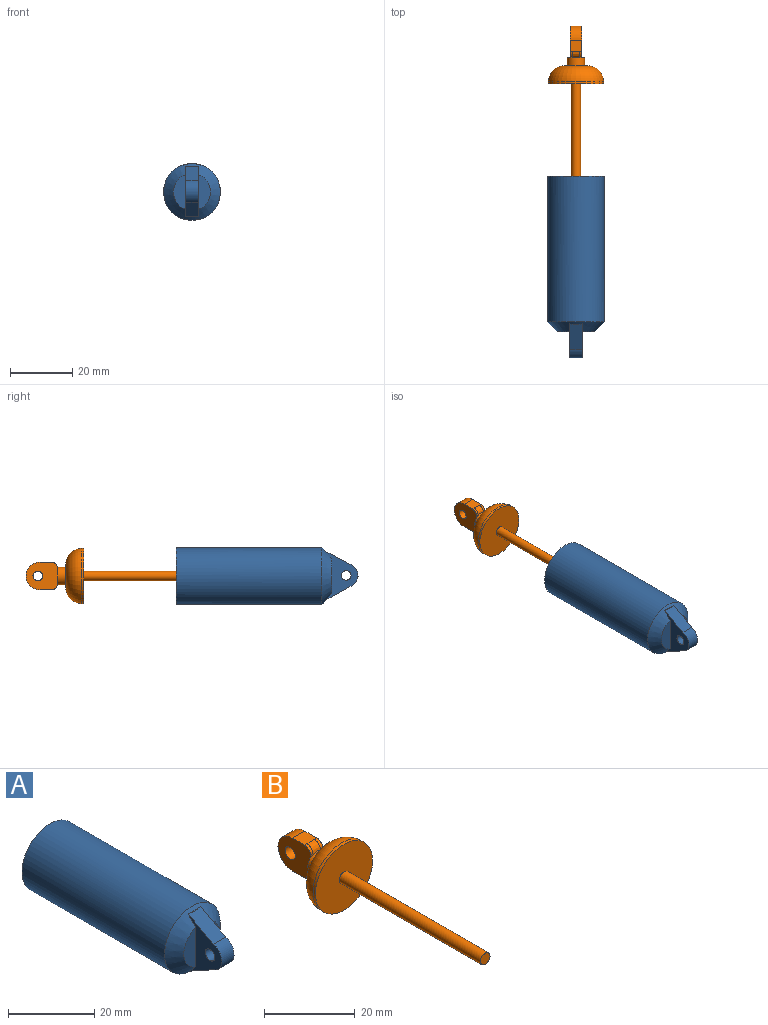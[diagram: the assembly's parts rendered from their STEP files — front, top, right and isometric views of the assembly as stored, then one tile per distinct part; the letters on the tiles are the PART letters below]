
ASSEMBLY  parts=2 mates=1
PART A: 15 faces, bbox 18.4x58.7x18.4 mm
  f0: plane 16.27x11.16mm, normal (1,0,0), area 70.3mm2, adj f1,f3,f7,f8,f9,f10
  f1: plane 11.23x3.94mm, normal (0,-1,0), area 32.2mm2, adj f0,f3
  f2: plane 11.23x3.94mm, normal (0,-1,0), area 32.2mm2, adj f3,f6
  f3: cone r=5.97mm half-angle=45deg, axis (0,1,0), area 187.2mm2, adj f0,f1,f2,f4,f6,f11,f12
  f4: cylinder r=9.14mm len=46.86mm, axis (0,1,0), area 2692.4mm2, adj f3,f5
  f5: plane 18.29x18.29mm, normal (0,1,0), area 255.4mm2, adj f4,f13
  f6: plane 16.27x11.16mm, normal (-1,0,0), area 70.3mm2, adj f2,f3,f7,f8,f9,f10
  f7: cylinder r=1.56mm len=4.06mm, axis (1,0,0), area 39.9mm2, adj f0,f6
  f8: cylinder r=3.81mm len=7.26mm, axis (1,0,0), area 39.1mm2, adj f0,f6,f9,f10
  f9: plane 8.37x4.44mm, normal (0,-0.47,0.88), area 38.5mm2, adj f0,f6,f8,f11
  f10: plane 8.04x4.44mm, normal (0,-0.48,-0.88), area 37.3mm2, adj f0,f6,f8,f12
  f11: plane 4.08x0.26mm, normal (0,0,-1), area 0.7mm2, adj f3,f9
  f12: plane 4.08x0.27mm, normal (0,0,1), area 0.7mm2, adj f3,f10
  f13: cylinder r=1.52mm len=34.54mm, axis (0,1,0), area 330.8mm2, adj f5,f14
  f14: plane 3.05x3.05mm, normal (0,1,0), area 7.3mm2, adj f13
PART B: 29 faces, bbox 17.8x62.6x17.8 mm
  f0: plane 0.74x0.5mm, normal (0,-1,0), area 0.2mm2, adj f10,f15,f25
  f1: plane 0.74x0.5mm, normal (0,-1,0), area 0.2mm2, adj f10,f13,f22
  f2: plane 4.09x0.89mm, normal (0,1,0), area 2.5mm2, adj f10,f13
  f3: plane 4.09x0.89mm, normal (0,1,0), area 2.5mm2, adj f10,f15
  f4: cylinder r=1.5mm len=43.94mm, axis (0,-1,0), area 413.8mm2, adj f5,f8
  f5: plane 3x3mm, normal (0,-1,0), area 7.1mm2, adj f4
  f6: cylinder r=8.89mm len=17.78mm, axis (0,-1,0), area 41.1mm2, adj f8,f9
  f7: plane 7.62x7.62mm, normal (0,1,0), area 21.1mm2, adj f9,f10
  f8: plane 17.78x17.78mm, normal (0,-1,0), area 241.2mm2, adj f4,f6
  f9: torus R=3.81mm, axis (0,1,0), area 353.2mm2, adj f6,f7
  f10: cylinder r=2.79mm len=5.59mm, axis (0,-1,0), area 46.8mm2, adj f0,f1,f2,f3,f7,f11,f12,f21
  f11: plane 0.74x0.5mm, normal (0,-1,0), area 0.2mm2, adj f10,f13,f23
  f12: plane 0.74x0.5mm, normal (0,-1,0), area 0.2mm2, adj f10,f15,f20
  f13: plane 10.16x8.89mm, normal (1,0,0), area 72.3mm2, adj f1,f2,f11,f14,f16,f17,f18,f19
  f14: plane 3.81x3.74mm, normal (0,0,-1), area 14.2mm2, adj f13,f15,f18,f23,f24,f25
  f15: plane 10.16x8.89mm, normal (-1,0,0), area 72.3mm2, adj f0,f3,f12,f14,f16,f17,f18,f19
  f16: plane 3.81x3.74mm, normal (0,0,1), area 14.2mm2, adj f13,f15,f19,f20,f21,f22
  f17: cylinder r=1.56mm len=3.81mm, axis (1,0,0), area 37.4mm2, adj f13,f15
  f18: cylinder r=4.54mm len=4.54mm, axis (1,0,0), area 26.8mm2, adj f13,f14,f15,f19
  f19: cylinder r=4.54mm len=4.54mm, axis (-1,0,0), area 26.8mm2, adj f13,f15,f16,f18
  f20: cylinder r=1.91mm len=1.91mm, axis (1,0,0), area 2.2mm2, adj f12,f15,f16,f21
  f21: bspline ~3.62x2.3mm, area 6.6mm2, adj f10,f16,f20,f22
  f22: cylinder r=1.91mm len=1.91mm, axis (1,0,0), area 2.2mm2, adj f1,f13,f16,f21
  f23: cylinder r=1.91mm len=1.91mm, axis (-1,0,0), area 2.2mm2, adj f11,f13,f14,f24
  f24: bspline ~3.62x2.3mm, area 6.6mm2, adj f10,f14,f23,f25
  f25: cylinder r=1.91mm len=1.91mm, axis (-1,0,0), area 2.2mm2, adj f0,f14,f15,f24
  f26: plane 3x3mm, normal (0,1,0), area 7.1mm2, adj f27
  f27: cylinder r=1.5mm len=3mm, axis (0,-1,0), area 2.2mm2, adj f26,f28
  f28: plane 3x3mm, normal (0,-1,0), area 7.1mm2, adj f27
PLACE A rot(axis=(0.97,0.26,0),0deg) t=(-64.35,105.8,32.02)mm
PLACE B rot(axis=(0.97,0.26,0),0deg) t=(-64.35,104.27,32.02)mm
MATE slider A.f3 <-> B.f4  axis (0,1,0) through (-29.88,82.37,75.42)mm
